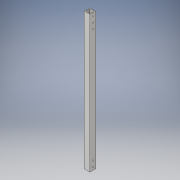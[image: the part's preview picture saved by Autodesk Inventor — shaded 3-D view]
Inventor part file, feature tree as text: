
AUTODESK INVENTOR PART (.ipt)
format: ipt  version: 2018 (Build 220112000, 112)  size: 129,024 bytes
history: native  units: in
note: dims shown in document units (in); Inventor stores cm internally (conversion verified against a paired STEP export)
features: extrude x3, sketch x3
ambient origin geometry x8: Origin, YZ Plane, XZ Plane, XY Plane, X Axis, Y Axis, Z Axis, Center Point
bodies: Solid1 (feature_tree)
feature tree (6):
  extrude  "Extrusion1"  Depth=1.0in
  extrude  "Extrusion2"  Depth=24.0in TaperAngle=0.0deg
  extrude  "Extrusion3"  Depth=1.0in
  sketch  "Sketch1"  dims[d0=1.0in d1=1.0in]
  sketch  "Sketch2"  dims[d2=0.125in d3=24.0in d4=0.0in]
  sketch  "Sketch3"  dims[d5=0.5in d6=1.0in d7=0.5in d8=1.0in d9=0.2031in d10=0.2031in d11=0.2031in d12=0.2031in d13=25.0in d14=0.0in d15=1.0in d16=0.2031in d17=5.0in d18=0.0in]
